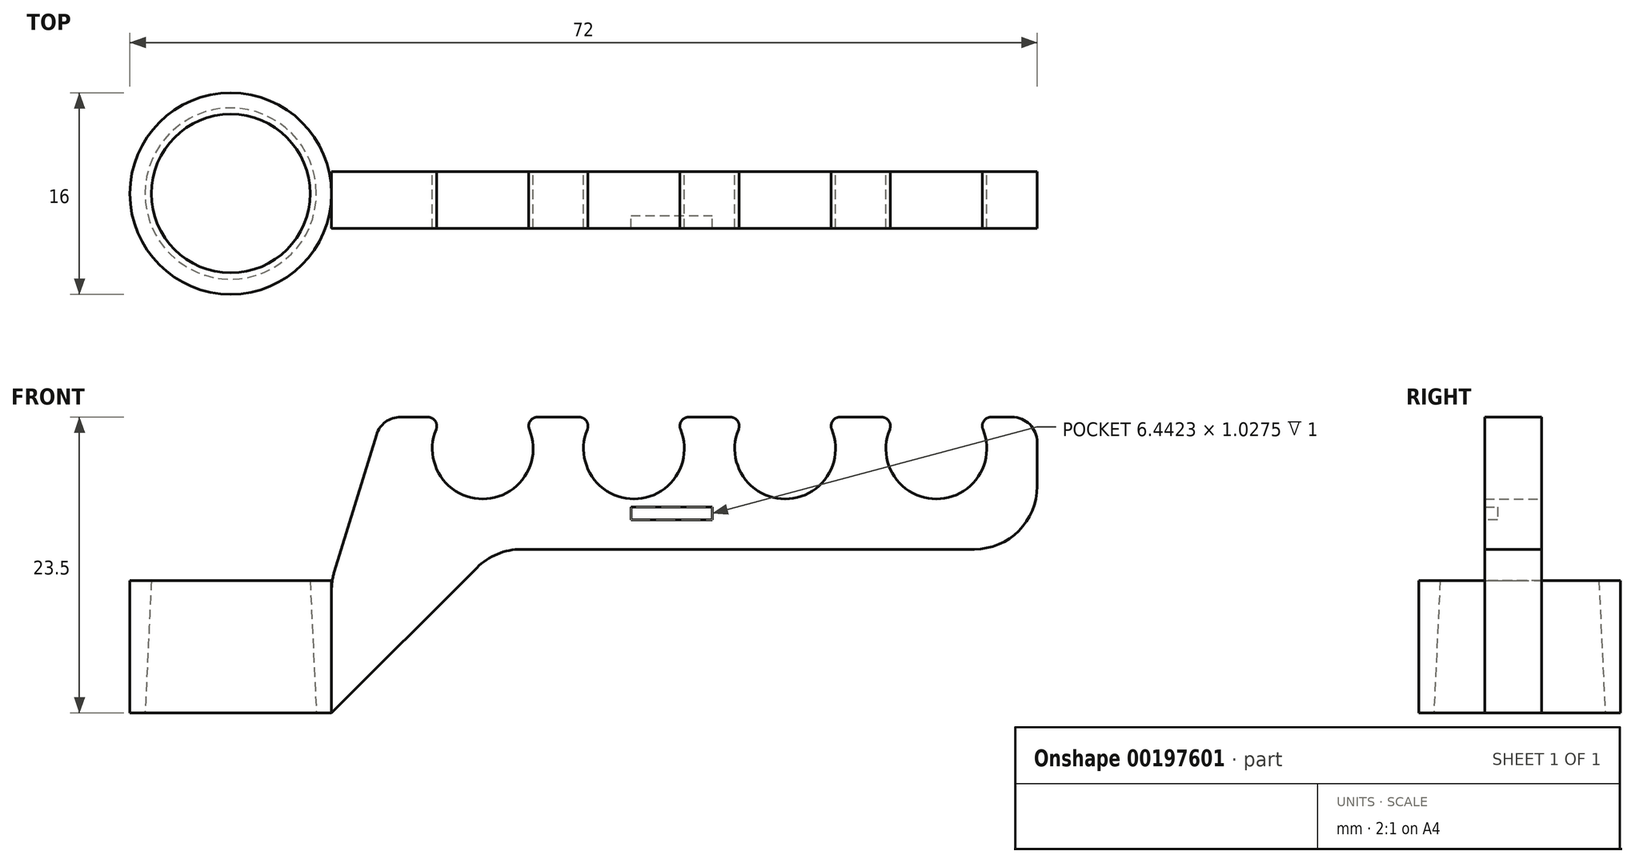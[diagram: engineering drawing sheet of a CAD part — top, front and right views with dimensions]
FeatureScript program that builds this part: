
annotation { "Feature Type Name" : "Feature", "Feature Type Description" : "" }
export const myFeature = defineFeature(function(context is Context, id is Id, definition is map)
    precondition{}
    {
        {
            var Q0;
            Q0=qCreatedBy(makeId("Top.planeOp"),FACE);
            var sketch = newSketch(context, id + "F0", { "sketchPlane" : qUnion([Q0])});
            skCircle(sketch, "E0", {"center": v(0, 0) * mm, "radius": 6.3 * mm});
            skCircle(sketch, "E1", {"center": v(0, 0) * mm, "radius": 8 * mm});
            skCircle(sketch, "E2", {"center": v(0, 0) * mm, "radius": 6.8 * mm});
            skSolve(sketch);
        }
        {
            var Q0;
            Q0=qCreatedBy(makeId("Front.planeOp"),FACE);
            var sketch = newSketch(context, id + "F1", { "sketchPlane" : qUnion([Q0])});
            skLineSegment(sketch, "E3.0", {"start": v(-6.8, 0) * mm, "end": v(6.8, 0) * mm});
            skLineSegment(sketch, "E4.0", {"start": v(-6.3, 0) * mm, "end": v(6.3, 0) * mm});
            skLineSegment(sketch, "E5.0", {"start": v(-8, 0) * mm, "end": v(-5.58, 0) * mm});
            skLineSegment(sketch, "E6", {"start": v(0, 0) * mm, "end": v(0, 10.5) * mm});
            skLineSegment(sketch, "E7.top", {"start": v(-8, 10.5) * mm, "end": v(-6.3, 10.5) * mm});
            skLineSegment(sketch, "E7.left", {"start": v(-8, 0) * mm, "end": v(-8, 10.5) * mm});
            skLineSegment(sketch, "E8", {"start": v(-6.3, 10.5) * mm, "end": v(-6.8, 0) * mm});
            skLineSegment(sketch, "E9.trimOffspring", {"start": v(0, 0) * mm, "end": v(8, 0) * mm});
            skSolve(sketch);
        }
        {
            var Q0;
            Q0=makeQuery(id+"F1.imprint","IMPRINT",FACE,{"disambiguationData":[TD([[makeQuery(id+"F1.imprint","IMPRINT",EDGE,{"derivedFrom":sQuery(id+"F1.wireOp",EDGE,"E7.top")}),-1.0]])]});
            var Q1;
            Q1=sQuery(id+"F1.wireOp",EDGE,"E6");
            revolve(context, id + "F2", {"entities" : qUnion([Q0]), "axis" : qUnion([Q1]), "revolveType" : RevolveType.FULL});
        }
        {
            var Q0;
            Q0=qCreatedBy(makeId("Front.planeOp"),FACE);
            var sketch = newSketch(context, id + "F3", { "sketchPlane" : qUnion([Q0])});
            skLineSegment(sketch, "E10", {"start": v(8, 10.5) * mm, "end": v(8, 0) * mm});
            skLineSegment(sketch, "E11.0", {"start": v(8, 10.5) * mm, "end": v(-8, 10.5) * mm});
            skLineSegment(sketch, "E12.0", {"start": v(-8, 0) * mm, "end": v(8, 0) * mm});
            skLineSegment(sketch, "E13", {"start": v(0, 13) * mm, "end": v(41.13, 13) * mm, "construction": true});
            skLineSegment(sketch, "E14", {"start": v(0, 21) * mm, "end": v(40.48, 21) * mm, "construction": true});
            skLineSegment(sketch, "E15", {"start": v(20, 25.73) * mm, "end": v(20, 4.34) * mm, "construction": true});
            skCircle(sketch, "E16", {"center": v(20, 21) * mm, "radius": 4 * mm});
            skCircle(sketch, "E17.1.0.0", {"center": v(32, 21) * mm, "radius": 4 * mm});
            skCircle(sketch, "E17.2.0.0", {"center": v(44, 21) * mm, "radius": 4 * mm});
            skCircle(sketch, "E17.3.0.0", {"center": v(56, 21) * mm, "radius": 4 * mm});
            skLineSegment(sketch, "E17.direction1", {"start": v(20, 21) * mm, "end": v(32, 21) * mm, "construction": true});
            skLineSegment(sketch, "E18", {"start": v(12, 25.64) * mm, "end": v(12, 16.43) * mm, "construction": true});
            skLineSegment(sketch, "E19", {"start": v(12, 23.5) * mm, "end": v(68.02, 23.5) * mm});
            skLineSegment(sketch, "E20", {"start": v(64, 26.61) * mm, "end": v(64, 15.45) * mm, "construction": true});
            skLineSegment(sketch, "E21", {"start": v(12, 23.5) * mm, "end": v(8, 10.5) * mm});
            skLineSegment(sketch, "E22", {"start": v(22.25, 13) * mm, "end": v(41.13, 13) * mm});
            skLineSegment(sketch, "E23", {"start": v(64, 13) * mm, "end": v(64, 23.5) * mm});
            skLineSegment(sketch, "E24", {"start": v(8, 0) * mm, "end": v(21, 13) * mm});
            skPoint(sketch, "E25.orphan", {"position": v(22.25, 14.25) * mm});
            skLineSegment(sketch, "E26", {"start": v(21, 13) * mm, "end": v(22.25, 13) * mm});
            skLineSegment(sketch, "E27", {"start": v(41.13, 13) * mm, "end": v(64, 13) * mm});
            skLineSegment(sketch, "E28.bottom", {"start": v(8, 10.5) * mm, "end": v(7.8, 10.5) * mm});
            skLineSegment(sketch, "E28.top", {"start": v(8, 0) * mm, "end": v(7.8, 0) * mm});
            skLineSegment(sketch, "E28.right", {"start": v(7.8, 10.5) * mm, "end": v(7.8, 0) * mm});
            skSolve(sketch);
        }
        {
            var Q0;
            {var subQ0=sQuery(id+"F3.wireOp",EDGE,"E21");Q0=makeQuery(id+"F3.imprint","IMPRINT",FACE,{"disambiguationData":[TD([[makeQuery(id+"F3.imprint","IMPRINT",EDGE,{"derivedFrom":subQ0}),1.0]])]});}
            var Q1;
            Q1=makeQuery(id+"F3.imprint","IMPRINT",FACE,{"disambiguationData":[TD([[makeQuery(id+"F3.imprint","IMPRINT",EDGE,{"derivedFrom":sQuery(id+"F3.wireOp",EDGE,"E28.bottom")}),1.0]])]});
            extrude(context, id + "F4", {"entities" : qUnion([Q0, Q1]), "operationType" : NewBodyOperationType.ADD, "endBound" : BoundingType.SYMMETRIC, "depth" : 3.5 * mm});
        }
        {
            var Q0;
            Q0=makeQuery(id+"F4.boolean.opBoolean","INTERSECT",EDGE,{"derivedFrom":[makeQuery(id+"F2.opRevolve","SWEPT_FACE",FACE,{"disambiguationData":[OSD([sQuery(id+"F1.wireOp",EDGE,"E7.left")])]}),makeQuery(id+"F4.opExtrude","CAP_FACE",FACE,{"disambiguationData":[OSD([sQuery(id+"F3.wireOp",EDGE,"E16"),sQuery(id+"F3.wireOp",EDGE,"E17.1.0.0"),sQuery(id+"F3.wireOp",EDGE,"E17.2.0.0"),sQuery(id+"F3.wireOp",EDGE,"E17.3.0.0"),sQuery(id+"F3.wireOp",EDGE,"E19"),sQuery(id+"F3.wireOp",EDGE,"E21"),sQuery(id+"F3.wireOp",EDGE,"E22"),sQuery(id+"F3.wireOp",EDGE,"E23"),sQuery(id+"F3.wireOp",EDGE,"E24"),sQuery(id+"F3.wireOp",EDGE,"E26"),sQuery(id+"F3.wireOp",EDGE,"E27"),sQuery(id+"F3.wireOp",EDGE,"E28.bottom"),sQuery(id+"F3.wireOp",EDGE,"E28.top"),sQuery(id+"F3.wireOp",EDGE,"E28.right")])],"isStart":true})]});
            var Q1;
            Q1=makeQuery(id+"F4.boolean.opBoolean","INTERSECT",EDGE,{"derivedFrom":[makeQuery(id+"F2.opRevolve","SWEPT_FACE",FACE,{"disambiguationData":[OSD([sQuery(id+"F1.wireOp",EDGE,"E7.left")])]}),makeQuery(id+"F4.opExtrude","CAP_FACE",FACE,{"disambiguationData":[OSD([sQuery(id+"F3.wireOp",EDGE,"E16"),sQuery(id+"F3.wireOp",EDGE,"E17.1.0.0"),sQuery(id+"F3.wireOp",EDGE,"E17.2.0.0"),sQuery(id+"F3.wireOp",EDGE,"E17.3.0.0"),sQuery(id+"F3.wireOp",EDGE,"E19"),sQuery(id+"F3.wireOp",EDGE,"E21"),sQuery(id+"F3.wireOp",EDGE,"E22"),sQuery(id+"F3.wireOp",EDGE,"E23"),sQuery(id+"F3.wireOp",EDGE,"E24"),sQuery(id+"F3.wireOp",EDGE,"E26"),sQuery(id+"F3.wireOp",EDGE,"E27"),sQuery(id+"F3.wireOp",EDGE,"E28.bottom"),sQuery(id+"F3.wireOp",EDGE,"E28.top"),sQuery(id+"F3.wireOp",EDGE,"E28.right")])],"isStart":false})]});
            var Q2;
            Q2=makeQuery(id+"F4.opExtrude","SWEPT_EDGE",EDGE,{"disambiguationData":[OSD([sQuery(id+"F3.wireOp",EDGE,"E24"),sQuery(id+"F3.wireOp",EDGE,"E26")])]});
            var Q3;
            Q3=makeQuery(id+"F4.opExtrude","SWEPT_EDGE",EDGE,{"disambiguationData":[OSD([sQuery(id+"F3.wireOp",EDGE,"E23"),sQuery(id+"F3.wireOp",EDGE,"E27")])]});
            fillet(context, id + "F5", {"entities" : qUnion([Q0, Q1, Q2, Q3]), "radius" : 5 * mm, "tangentPropagation" : true, "allowEdgeOverflow" : false});
        }
        {
            var Q0;
            Q0=makeQuery(id+"F4.opExtrude","SWEPT_EDGE",EDGE,{"disambiguationData":[OSD([sQuery(id+"F3.wireOp",EDGE,"E19"),sQuery(id+"F3.wireOp",EDGE,"E21")])]});
            var Q1;
            Q1=makeQuery(id+"F4.opExtrude","SWEPT_EDGE",EDGE,{"disambiguationData":[OSD([sQuery(id+"F3.wireOp",EDGE,"E19"),sQuery(id+"F3.wireOp",EDGE,"E23")])]});
            fillet(context, id + "F6", {"entities" : qUnion([Q0, Q1]), "radius" : 2 * mm, "tangentPropagation" : true, "allowEdgeOverflow" : false});
        }
        {
            var Q0;
            {var subQ0=sQuery(id+"F3.wireOp",EDGE,"E19");var subQ1=sQuery(id+"F3.wireOp",EDGE,"E16");Q0=makeQuery(id+"F4.opExtrude","SWEPT_EDGE",EDGE,{"disambiguationData":[OSD([subQ1,subQ0]),TDD([makeQuery(id+"F3.imprint","INTERSECT",VERTEX,{"disambiguationData":[OD(1.0)],"derivedFrom":[subQ1,subQ0]})])]});}
            var Q1;
            {var subQ0=sQuery(id+"F3.wireOp",EDGE,"E19");var subQ1=sQuery(id+"F3.wireOp",EDGE,"E16");Q1=makeQuery(id+"F4.opExtrude","SWEPT_EDGE",EDGE,{"disambiguationData":[OSD([subQ1,subQ0]),TDD([makeQuery(id+"F3.imprint","INTERSECT",VERTEX,{"disambiguationData":[OD(0.0)],"derivedFrom":[subQ1,subQ0]})])]});}
            var Q2;
            {var subQ0=sQuery(id+"F3.wireOp",EDGE,"E19");var subQ1=sQuery(id+"F3.wireOp",EDGE,"E17.1.0.0");Q2=makeQuery(id+"F4.opExtrude","SWEPT_EDGE",EDGE,{"disambiguationData":[OSD([subQ1,subQ0]),TDD([makeQuery(id+"F3.imprint","INTERSECT",VERTEX,{"disambiguationData":[OD(0.0)],"derivedFrom":[subQ1,subQ0]})])]});}
            var Q3;
            {var subQ0=sQuery(id+"F3.wireOp",EDGE,"E19");var subQ1=sQuery(id+"F3.wireOp",EDGE,"E17.2.0.0");Q3=makeQuery(id+"F4.opExtrude","SWEPT_EDGE",EDGE,{"disambiguationData":[OSD([subQ1,subQ0]),TDD([makeQuery(id+"F3.imprint","INTERSECT",VERTEX,{"disambiguationData":[OD(0.0)],"derivedFrom":[subQ1,subQ0]})])]});}
            var Q4;
            {var subQ0=sQuery(id+"F3.wireOp",EDGE,"E19");var subQ1=sQuery(id+"F3.wireOp",EDGE,"E17.3.0.0");Q4=makeQuery(id+"F4.opExtrude","SWEPT_EDGE",EDGE,{"disambiguationData":[OSD([subQ1,subQ0]),TDD([makeQuery(id+"F3.imprint","INTERSECT",VERTEX,{"disambiguationData":[OD(0.0)],"derivedFrom":[subQ1,subQ0]})])]});}
            var Q5;
            {var subQ0=sQuery(id+"F3.wireOp",EDGE,"E19");var subQ1=sQuery(id+"F3.wireOp",EDGE,"E17.1.0.0");Q5=makeQuery(id+"F4.opExtrude","SWEPT_EDGE",EDGE,{"disambiguationData":[OSD([subQ1,subQ0]),TDD([makeQuery(id+"F3.imprint","INTERSECT",VERTEX,{"disambiguationData":[OD(1.0)],"derivedFrom":[subQ1,subQ0]})])]});}
            var Q6;
            {var subQ0=sQuery(id+"F3.wireOp",EDGE,"E19");var subQ1=sQuery(id+"F3.wireOp",EDGE,"E17.2.0.0");Q6=makeQuery(id+"F4.opExtrude","SWEPT_EDGE",EDGE,{"disambiguationData":[OSD([subQ1,subQ0]),TDD([makeQuery(id+"F3.imprint","INTERSECT",VERTEX,{"disambiguationData":[OD(1.0)],"derivedFrom":[subQ1,subQ0]})])]});}
            var Q7;
            {var subQ0=sQuery(id+"F3.wireOp",EDGE,"E19");var subQ1=sQuery(id+"F3.wireOp",EDGE,"E17.3.0.0");Q7=makeQuery(id+"F4.opExtrude","SWEPT_EDGE",EDGE,{"disambiguationData":[OSD([subQ1,subQ0]),TDD([makeQuery(id+"F3.imprint","INTERSECT",VERTEX,{"disambiguationData":[OD(1.0)],"derivedFrom":[subQ1,subQ0]})])]});}
            fillet(context, id + "F7", {"entities" : qUnion([Q0, Q1, Q2, Q3, Q4, Q5, Q6, Q7]), "radius" : .71 * mm, "tangentPropagation" : true, "allowEdgeOverflow" : false});
        }
        {
            var Q0;
            Q0=makeQuery(id+"F4.opExtrude","CAP_FACE",FACE,{"disambiguationData":[OSD([sQuery(id+"F3.wireOp",EDGE,"E16"),sQuery(id+"F3.wireOp",EDGE,"E17.1.0.0"),sQuery(id+"F3.wireOp",EDGE,"E17.2.0.0"),sQuery(id+"F3.wireOp",EDGE,"E17.3.0.0"),sQuery(id+"F3.wireOp",EDGE,"E19"),sQuery(id+"F3.wireOp",EDGE,"E21"),sQuery(id+"F3.wireOp",EDGE,"E22"),sQuery(id+"F3.wireOp",EDGE,"E23"),sQuery(id+"F3.wireOp",EDGE,"E24"),sQuery(id+"F3.wireOp",EDGE,"E26"),sQuery(id+"F3.wireOp",EDGE,"E27"),sQuery(id+"F3.wireOp",EDGE,"E28.bottom"),sQuery(id+"F3.wireOp",EDGE,"E28.top"),sQuery(id+"F3.wireOp",EDGE,"E28.right")])],"isStart":false});
            var sketch = newSketch(context, id + "F8", { "sketchPlane" : qUnion([Q0])});
            skFitSpline(sketch, "E29", {"points": [v(35.71, 16.35) * mm, v(35.78, 16.55) * mm, v(35.85, 16.65) * mm, v(35.98, 16.75) * mm, v(36.12, 16.8) * mm, v(36.24, 16.8) * mm, v(42.55, 16.82) * mm, v(42.65, 16.78) * mm, v(42.7, 16.65) * mm, v(42.65, 16.52) * mm, v(42.55, 16.36) * mm, v(42.42, 16.32) * mm, v(42.3, 16.26) * mm, v(42.08, 15.9) * mm, v(41.89, 15.83) * mm, v(41.78, 15.76) * mm, v(41.62, 15.48) * mm, v(41.45, 15.38) * mm, v(38.77, 14.57) * mm, v(38.7, 14.56) * mm, v(38.62, 14.38) * mm, v(38.56, 14.27) * mm, v(38.18, 14.06) * mm, v(38.06, 14.02) * mm, v(35.9, 13.44) * mm, v(35.75, 13.44) * mm, v(35.65, 13.48) * mm, v(35.59, 13.53) * mm, v(35, 14.06) * mm, v(34.97, 14.05) * mm, v(34.9, 14.03) * mm, v(34.85, 14) * mm, v(34.31, 13.47) * mm, v(34.24, 13.44) * mm, v(34.16, 13.44) * mm, v(31.77, 14.07) * mm, v(31.41, 14.28) * mm, v(31.3, 14.48) * mm, v(31.22, 14.57) * mm, v(31.12, 14.6) * mm, v(28.44, 15.4) * mm, v(28.33, 15.52) * mm, v(28.2, 15.88) * mm, v(28.14, 15.83) * mm, v(28.02, 15.85) * mm, v(27.94, 15.87) * mm, v(27.88, 15.92) * mm, v(27.69, 16.27) * mm, v(27.65, 16.3) * mm, v(27.51, 16.3) * mm, v(27.46, 16.32) * mm, v(27.28, 16.62) * mm, v(27.28, 16.7) * mm, v(27.33, 16.77) * mm, v(27.4, 16.8) * mm, v(27.46, 16.8) * mm, v(33.8, 16.81) * mm, v(33.85, 16.81) * mm, v(33.97, 16.77) * mm, v(34.17, 16.6) * mm, v(34.2, 16.5) * mm, v(34.25, 16.4) * mm, v(34.26, 16.34) * mm, v(34.33, 16.34) * mm, v(35.58, 16.34) * mm, v(35.71, 16.35) * mm]});
            skFitSpline(sketch, "E30", {"points": [v(30.68, 16.8) * mm, v(30.83, 16.69) * mm, v(30.9, 16.62) * mm, v(30.99, 16.5) * mm, v(31.06, 16.33) * mm, v(31.28, 16.02) * mm, v(31.53, 15.67) * mm, v(31.6, 15.6) * mm, v(32.13, 15.09) * mm, v(32.73, 14.67) * mm, v(33.36, 14.37) * mm, v(33.87, 14.2) * mm, v(34.55, 14.1) * mm, v(35, 14.06) * mm, v(35.61, 14.1) * mm, v(36.24, 14.24) * mm, v(36.81, 14.44) * mm, v(37.3, 14.7) * mm, v(37.8, 15.05) * mm, v(38.1, 15.33) * mm, v(38.48, 15.75) * mm, v(38.72, 16.05) * mm, v(38.93, 16.39) * mm, v(39.08, 16.63) * mm, v(39.22, 16.76) * mm, v(39.4, 16.82) * mm, v(39.46, 16.82) * mm], "startDerivative": vector(6.61, -4.14) * mm, "endDerivative": vector(2.94, -0.27) * mm});
            skLineSegment(sketch, "E31.bottom", {"start": v(31.76, 16.35) * mm, "end": v(38.2, 16.35) * mm});
            skLineSegment(sketch, "E31.top", {"start": v(31.76, 15.33) * mm, "end": v(38.2, 15.33) * mm});
            skLineSegment(sketch, "E31.left", {"start": v(31.76, 16.35) * mm, "end": v(31.76, 15.33) * mm});
            skLineSegment(sketch, "E31.right", {"start": v(38.2, 16.35) * mm, "end": v(38.2, 15.33) * mm});
            skLineSegment(sketch, "E32", {"start": v(27.69, 16.27) * mm, "end": v(31.76, 16.35) * mm});
            skLineSegment(sketch, "E33", {"start": v(31.76, 16.1) * mm, "end": v(28.2, 15.88) * mm});
            skLineSegment(sketch, "E34", {"start": v(31.76, 15.88) * mm, "end": v(28.44, 15.4) * mm});
            skLineSegment(sketch, "E35", {"start": v(31.76, 15.67) * mm, "end": v(29.25, 15.15) * mm});
            skLineSegment(sketch, "E36", {"start": v(31.76, 15.33) * mm, "end": v(30.28, 14.84) * mm});
            skLineSegment(sketch, "E37", {"start": v(32.82, 15.33) * mm, "end": v(31.22, 14.57) * mm});
            skLineSegment(sketch, "E38", {"start": v(33.59, 15.33) * mm, "end": v(31.77, 14.07) * mm});
            skLineSegment(sketch, "E39", {"start": v(34.05, 15.33) * mm, "end": v(32.59, 13.83) * mm});
            skLineSegment(sketch, "E40", {"start": v(34.4, 15.33) * mm, "end": v(33.39, 13.61) * mm});
            skLineSegment(sketch, "E41", {"start": v(34.73, 15.33) * mm, "end": v(34.16, 13.44) * mm});
            skLineSegment(sketch, "E42", {"start": v(34.98, 15.33) * mm, "end": v(34.97, 14.05) * mm});
            skLineSegment(sketch, "E43", {"start": v(35.26, 15.33) * mm, "end": v(35.81, 13.43) * mm});
            skLineSegment(sketch, "E44", {"start": v(35.61, 15.33) * mm, "end": v(36.58, 13.6) * mm});
            skLineSegment(sketch, "E45", {"start": v(35.96, 15.33) * mm, "end": v(37.37, 13.83) * mm});
            skLineSegment(sketch, "E46", {"start": v(36.38, 15.33) * mm, "end": v(38.18, 14.06) * mm});
            skLineSegment(sketch, "E47", {"start": v(37.14, 15.33) * mm, "end": v(38.77, 14.57) * mm});
            skLineSegment(sketch, "E48", {"start": v(38.2, 15.33) * mm, "end": v(39.77, 14.85) * mm});
            skLineSegment(sketch, "E49", {"start": v(38.2, 15.65) * mm, "end": v(40.68, 15.13) * mm});
            skLineSegment(sketch, "E50", {"start": v(38.2, 15.87) * mm, "end": v(41.57, 15.43) * mm});
            skLineSegment(sketch, "E51", {"start": v(38.2, 16.1) * mm, "end": v(42.02, 15.86) * mm});
            skLineSegment(sketch, "E52", {"start": v(38.2, 16.3) * mm, "end": v(42.35, 16.3) * mm});
            skSolve(sketch);
        }
        {
            var Q0;
            {var subQ0=sQuery(id+"F8.wireOp",EDGE,"E36");Q0=makeQuery(id+"F8.imprint","IMPRINT",FACE,{"disambiguationData":[TD([[makeQuery(id+"F8.imprint","IMPRINT",EDGE,{"derivedFrom":subQ0}),-1.0]])]});}
            var Q1;
            {var subQ0=sQuery(id+"F8.wireOp",EDGE,"E46");var subQ1=sQuery(id+"F8.wireOp",EDGE,"E29");var subQ2=makeQuery(id+"F8.imprint","INTERSECT",VERTEX,{"derivedFrom":[subQ1,subQ0]});Q1=makeQuery(id+"F8.imprint","IMPRINT",FACE,{"disambiguationData":[TD([[makeQuery(id+"F8.imprint","IMPRINT",EDGE,{"disambiguationData":[TD([[subQ2,1.0]])],"derivedFrom":subQ1}),-1.0]])]});}
            var Q2;
            {var subQ0=sQuery(id+"F8.wireOp",EDGE,"E38");var subQ1=sQuery(id+"F8.wireOp",EDGE,"E29");var subQ2=makeQuery(id+"F8.imprint","INTERSECT",VERTEX,{"derivedFrom":[subQ1,subQ0]});Q2=makeQuery(id+"F8.imprint","IMPRINT",FACE,{"disambiguationData":[TD([[makeQuery(id+"F8.imprint","IMPRINT",EDGE,{"disambiguationData":[TD([[subQ2,1.0]])],"derivedFrom":subQ1}),-1.0]])]});}
            var Q3;
            {var subQ0=sQuery(id+"F8.wireOp",EDGE,"E44");var subQ1=sQuery(id+"F8.wireOp",EDGE,"E30");var subQ2=makeQuery(id+"F8.imprint","INTERSECT",VERTEX,{"derivedFrom":[subQ1,subQ0]});Q3=makeQuery(id+"F8.imprint","IMPRINT",FACE,{"disambiguationData":[TD([[makeQuery(id+"F8.imprint","IMPRINT",EDGE,{"disambiguationData":[TD([[subQ2,-1.0]])],"derivedFrom":subQ1}),1.0]])]});}
            var Q4;
            {var subQ0=sQuery(id+"F8.wireOp",EDGE,"E39");var subQ1=sQuery(id+"F8.wireOp",EDGE,"E29");var subQ2=makeQuery(id+"F8.imprint","INTERSECT",VERTEX,{"derivedFrom":[subQ1,subQ0]});Q4=makeQuery(id+"F8.imprint","IMPRINT",FACE,{"disambiguationData":[TD([[makeQuery(id+"F8.imprint","IMPRINT",EDGE,{"disambiguationData":[TD([[subQ2,1.0]])],"derivedFrom":subQ1}),-1.0]])]});}
            var Q5;
            {var subQ0=sQuery(id+"F8.wireOp",EDGE,"E43");var subQ1=sQuery(id+"F8.wireOp",EDGE,"E30");var subQ2=makeQuery(id+"F8.imprint","INTERSECT",VERTEX,{"derivedFrom":[subQ1,subQ0]});Q5=makeQuery(id+"F8.imprint","IMPRINT",FACE,{"disambiguationData":[TD([[makeQuery(id+"F8.imprint","IMPRINT",EDGE,{"disambiguationData":[TD([[subQ2,-1.0]])],"derivedFrom":subQ1}),1.0]])]});}
            var Q6;
            {var subQ0=sQuery(id+"F8.wireOp",EDGE,"E30");var subQ1=sQuery(id+"F8.wireOp",EDGE,"E29");var subQ2=makeQuery(id+"F8.imprint","INTERSECT",VERTEX,{"disambiguationData":[OD(0.0)],"derivedFrom":[subQ1,subQ0]});Q6=makeQuery(id+"F8.imprint","IMPRINT",FACE,{"disambiguationData":[TD([[makeQuery(id+"F8.imprint","IMPRINT",EDGE,{"disambiguationData":[TD([[subQ2,-1.0]])],"derivedFrom":subQ1}),-1.0]])]});}
            var Q7;
            {var subQ0=sQuery(id+"F8.wireOp",EDGE,"E41");var subQ1=sQuery(id+"F8.wireOp",EDGE,"E30");var subQ2=makeQuery(id+"F8.imprint","INTERSECT",VERTEX,{"derivedFrom":[subQ1,subQ0]});Q7=makeQuery(id+"F8.imprint","IMPRINT",FACE,{"disambiguationData":[TD([[makeQuery(id+"F8.imprint","IMPRINT",EDGE,{"disambiguationData":[TD([[subQ2,-1.0]])],"derivedFrom":subQ1}),1.0]])]});}
            var Q8;
            {var subQ0=sQuery(id+"F8.wireOp",EDGE,"E32");var subQ1=sQuery(id+"F8.wireOp",EDGE,"E30");var subQ2=makeQuery(id+"F8.imprint","INTERSECT",VERTEX,{"derivedFrom":[subQ1,subQ0]});Q8=makeQuery(id+"F8.imprint","IMPRINT",FACE,{"disambiguationData":[TD([[makeQuery(id+"F8.imprint","IMPRINT",EDGE,{"disambiguationData":[TD([[subQ2,-1.0]])],"derivedFrom":subQ1}),1.0]])]});}
            var Q9;
            {var subQ0=sQuery(id+"F8.wireOp",EDGE,"E48");Q9=makeQuery(id+"F8.imprint","IMPRINT",FACE,{"disambiguationData":[TD([[makeQuery(id+"F8.imprint","IMPRINT",EDGE,{"derivedFrom":subQ0}),-1.0]])]});}
            var Q10;
            {var subQ0=sQuery(id+"F8.wireOp",EDGE,"E32");var subQ1=sQuery(id+"F8.wireOp",EDGE,"E29");var subQ2=makeQuery(id+"F8.imprint","INTERSECT",VERTEX,{"derivedFrom":[subQ1,subQ0]});Q10=makeQuery(id+"F8.imprint","IMPRINT",FACE,{"disambiguationData":[TD([[makeQuery(id+"F8.imprint","IMPRINT",EDGE,{"disambiguationData":[TD([[subQ2,1.0]])],"derivedFrom":subQ1}),-1.0]])]});}
            var Q11;
            {var subQ0=sQuery(id+"F8.wireOp",EDGE,"E40");var subQ1=sQuery(id+"F8.wireOp",EDGE,"E30");var subQ2=makeQuery(id+"F8.imprint","INTERSECT",VERTEX,{"derivedFrom":[subQ1,subQ0]});Q11=makeQuery(id+"F8.imprint","IMPRINT",FACE,{"disambiguationData":[TD([[makeQuery(id+"F8.imprint","IMPRINT",EDGE,{"disambiguationData":[TD([[subQ2,-1.0]])],"derivedFrom":subQ1}),1.0]])]});}
            var Q12;
            {var subQ3=sQuery(id+"F8.wireOp",EDGE,"E29");var subQ7=sQuery(id+"F8.wireOp",EDGE,"E30");var subQ8=makeQuery(id+"F8.imprint","INTERSECT",VERTEX,{"disambiguationData":[OD(2.0)],"derivedFrom":[subQ3,subQ7]});Q12=makeQuery(id+"F8.imprint","IMPRINT",FACE,{"disambiguationData":[TD([[makeQuery(id+"F8.imprint","IMPRINT",EDGE,{"disambiguationData":[TD([[subQ8,1.0]])],"derivedFrom":subQ3}),-1.0]])]});}
            var Q13;
            {var subQ0=sQuery(id+"F8.wireOp",EDGE,"E48");Q13=makeQuery(id+"F8.imprint","IMPRINT",FACE,{"disambiguationData":[TD([[makeQuery(id+"F8.imprint","IMPRINT",EDGE,{"derivedFrom":subQ0}),1.0]])]});}
            var Q14;
            {var subQ0=sQuery(id+"F8.wireOp",EDGE,"E33");var subQ1=sQuery(id+"F8.wireOp",EDGE,"E29");var subQ2=makeQuery(id+"F8.imprint","INTERSECT",VERTEX,{"derivedFrom":[subQ1,subQ0]});Q14=makeQuery(id+"F8.imprint","IMPRINT",FACE,{"disambiguationData":[TD([[makeQuery(id+"F8.imprint","IMPRINT",EDGE,{"disambiguationData":[TD([[subQ2,1.0]])],"derivedFrom":subQ1}),-1.0]])]});}
            var Q15;
            {var subQ0=sQuery(id+"F8.wireOp",EDGE,"E39");var subQ1=sQuery(id+"F8.wireOp",EDGE,"E30");var subQ2=makeQuery(id+"F8.imprint","INTERSECT",VERTEX,{"derivedFrom":[subQ1,subQ0]});Q15=makeQuery(id+"F8.imprint","IMPRINT",FACE,{"disambiguationData":[TD([[makeQuery(id+"F8.imprint","IMPRINT",EDGE,{"disambiguationData":[TD([[subQ2,-1.0]])],"derivedFrom":subQ1}),1.0]])]});}
            var Q16;
            {var subQ0=sQuery(id+"F8.wireOp",EDGE,"E34");var subQ1=sQuery(id+"F8.wireOp",EDGE,"E29");var subQ2=makeQuery(id+"F8.imprint","INTERSECT",VERTEX,{"derivedFrom":[subQ1,subQ0]});Q16=makeQuery(id+"F8.imprint","IMPRINT",FACE,{"disambiguationData":[TD([[makeQuery(id+"F8.imprint","IMPRINT",EDGE,{"disambiguationData":[TD([[subQ2,1.0]])],"derivedFrom":subQ1}),-1.0]])]});}
            var Q17;
            {var subQ0=sQuery(id+"F8.wireOp",EDGE,"E46");var subQ1=sQuery(id+"F8.wireOp",EDGE,"E30");var subQ2=makeQuery(id+"F8.imprint","INTERSECT",VERTEX,{"derivedFrom":[subQ1,subQ0]});Q17=makeQuery(id+"F8.imprint","IMPRINT",FACE,{"disambiguationData":[TD([[makeQuery(id+"F8.imprint","IMPRINT",EDGE,{"disambiguationData":[TD([[subQ2,-1.0]])],"derivedFrom":subQ1}),1.0]])]});}
            var Q18;
            {var subQ0=sQuery(id+"F8.wireOp",EDGE,"E38");var subQ1=sQuery(id+"F8.wireOp",EDGE,"E30");var subQ2=makeQuery(id+"F8.imprint","INTERSECT",VERTEX,{"derivedFrom":[subQ1,subQ0]});Q18=makeQuery(id+"F8.imprint","IMPRINT",FACE,{"disambiguationData":[TD([[makeQuery(id+"F8.imprint","IMPRINT",EDGE,{"disambiguationData":[TD([[subQ2,-1.0]])],"derivedFrom":subQ1}),1.0]])]});}
            var Q19;
            {var subQ0=sQuery(id+"F8.wireOp",EDGE,"E36");Q19=makeQuery(id+"F8.imprint","IMPRINT",FACE,{"disambiguationData":[TD([[makeQuery(id+"F8.imprint","IMPRINT",EDGE,{"derivedFrom":subQ0}),1.0]])]});}
            var Q20;
            {var subQ0=sQuery(id+"F8.wireOp",EDGE,"E44");var subQ1=sQuery(id+"F8.wireOp",EDGE,"E29");var subQ2=makeQuery(id+"F8.imprint","INTERSECT",VERTEX,{"derivedFrom":[subQ1,subQ0]});Q20=makeQuery(id+"F8.imprint","IMPRINT",FACE,{"disambiguationData":[TD([[makeQuery(id+"F8.imprint","IMPRINT",EDGE,{"disambiguationData":[TD([[subQ2,1.0]])],"derivedFrom":subQ1}),-1.0]])]});}
            var Q21;
            {var subQ0=sQuery(id+"F8.wireOp",EDGE,"E37");var subQ1=sQuery(id+"F8.wireOp",EDGE,"E30");var subQ2=makeQuery(id+"F8.imprint","INTERSECT",VERTEX,{"derivedFrom":[subQ1,subQ0]});Q21=makeQuery(id+"F8.imprint","IMPRINT",FACE,{"disambiguationData":[TD([[makeQuery(id+"F8.imprint","IMPRINT",EDGE,{"disambiguationData":[TD([[subQ2,-1.0]])],"derivedFrom":subQ1}),1.0]])]});}
            var Q22;
            {var subQ5=sQuery(id+"F8.wireOp",EDGE,"E30");var subQ6=sQuery(id+"F8.wireOp",EDGE,"E29");var subQ9=makeQuery(id+"F8.imprint","INTERSECT",VERTEX,{"disambiguationData":[OD(3.0)],"derivedFrom":[subQ6,subQ5]});Q22=makeQuery(id+"F8.imprint","IMPRINT",FACE,{"disambiguationData":[TD([[makeQuery(id+"F8.imprint","IMPRINT",EDGE,{"disambiguationData":[TD([[subQ9,-1.0]])],"derivedFrom":subQ6}),-1.0]])]});}
            var Q23;
            {var subQ0=sQuery(id+"F8.wireOp",EDGE,"E45");var subQ1=sQuery(id+"F8.wireOp",EDGE,"E29");var subQ2=makeQuery(id+"F8.imprint","INTERSECT",VERTEX,{"derivedFrom":[subQ1,subQ0]});Q23=makeQuery(id+"F8.imprint","IMPRINT",FACE,{"disambiguationData":[TD([[makeQuery(id+"F8.imprint","IMPRINT",EDGE,{"disambiguationData":[TD([[subQ2,1.0]])],"derivedFrom":subQ1}),-1.0]])]});}
            var Q24;
            {var subQ0=sQuery(id+"F8.wireOp",EDGE,"E30");var subQ1=sQuery(id+"F8.wireOp",EDGE,"E29");var subQ2=makeQuery(id+"F8.imprint","INTERSECT",VERTEX,{"disambiguationData":[OD(1.0)],"derivedFrom":[subQ1,subQ0]});Q24=makeQuery(id+"F8.imprint","IMPRINT",FACE,{"disambiguationData":[TD([[makeQuery(id+"F8.imprint","IMPRINT",EDGE,{"disambiguationData":[TD([[subQ2,1.0]])],"derivedFrom":subQ1}),-1.0]])]});}
            var Q25;
            {var subQ0=sQuery(id+"F8.wireOp",EDGE,"E47");var subQ1=sQuery(id+"F8.wireOp",EDGE,"E30");var subQ2=makeQuery(id+"F8.imprint","INTERSECT",VERTEX,{"derivedFrom":[subQ1,subQ0]});Q25=makeQuery(id+"F8.imprint","IMPRINT",FACE,{"disambiguationData":[TD([[makeQuery(id+"F8.imprint","IMPRINT",EDGE,{"disambiguationData":[TD([[subQ2,-1.0]])],"derivedFrom":subQ1}),1.0]])]});}
            var Q26;
            {var subQ0=sQuery(id+"F8.wireOp",EDGE,"E37");var subQ1=sQuery(id+"F8.wireOp",EDGE,"E29");var subQ2=makeQuery(id+"F8.imprint","INTERSECT",VERTEX,{"derivedFrom":[subQ1,subQ0]});Q26=makeQuery(id+"F8.imprint","IMPRINT",FACE,{"disambiguationData":[TD([[makeQuery(id+"F8.imprint","IMPRINT",EDGE,{"disambiguationData":[TD([[subQ2,1.0]])],"derivedFrom":subQ1}),-1.0]])]});}
            var Q27;
            {var subQ0=sQuery(id+"F8.wireOp",EDGE,"E45");var subQ1=sQuery(id+"F8.wireOp",EDGE,"E30");var subQ2=makeQuery(id+"F8.imprint","INTERSECT",VERTEX,{"derivedFrom":[subQ1,subQ0]});Q27=makeQuery(id+"F8.imprint","IMPRINT",FACE,{"disambiguationData":[TD([[makeQuery(id+"F8.imprint","IMPRINT",EDGE,{"disambiguationData":[TD([[subQ2,-1.0]])],"derivedFrom":subQ1}),1.0]])]});}
            var Q28;
            {var subQ0=sQuery(id+"F8.wireOp",EDGE,"E30");var subQ1=sQuery(id+"F8.wireOp",EDGE,"E29");var subQ2=makeQuery(id+"F8.imprint","INTERSECT",VERTEX,{"disambiguationData":[OD(0.0)],"derivedFrom":[subQ1,subQ0]});Q28=makeQuery(id+"F8.imprint","IMPRINT",FACE,{"disambiguationData":[TD([[makeQuery(id+"F8.imprint","IMPRINT",EDGE,{"disambiguationData":[TD([[subQ2,1.0]])],"derivedFrom":subQ1}),-1.0]])]});}
            var Q29;
            {var subQ0=sQuery(id+"F8.wireOp",EDGE,"E31.bottom");var subQ1=sQuery(id+"F8.wireOp",EDGE,"E29");var subQ2=makeQuery(id+"F8.imprint","INTERSECT",VERTEX,{"disambiguationData":[OD(0.0)],"derivedFrom":[subQ1,subQ0]});Q29=makeQuery(id+"F8.imprint","IMPRINT",FACE,{"disambiguationData":[TD([[makeQuery(id+"F8.imprint","IMPRINT",EDGE,{"disambiguationData":[TD([[subQ2,-1.0]])],"derivedFrom":subQ1}),1.0]])]});}
            var Q30;
            {var subQ0=sQuery(id+"F8.wireOp",EDGE,"E50");var subQ1=sQuery(id+"F8.wireOp",EDGE,"E29");var subQ2=makeQuery(id+"F8.imprint","INTERSECT",VERTEX,{"derivedFrom":[subQ1,subQ0]});Q30=makeQuery(id+"F8.imprint","IMPRINT",FACE,{"disambiguationData":[TD([[makeQuery(id+"F8.imprint","IMPRINT",EDGE,{"disambiguationData":[TD([[subQ2,1.0]])],"derivedFrom":subQ1}),-1.0]])]});}
            var Q31;
            {var subQ0=sQuery(id+"F8.wireOp",EDGE,"E51");var subQ1=sQuery(id+"F8.wireOp",EDGE,"E29");var subQ2=makeQuery(id+"F8.imprint","INTERSECT",VERTEX,{"derivedFrom":[subQ1,subQ0]});Q31=makeQuery(id+"F8.imprint","IMPRINT",FACE,{"disambiguationData":[TD([[makeQuery(id+"F8.imprint","IMPRINT",EDGE,{"disambiguationData":[TD([[subQ2,1.0]])],"derivedFrom":subQ1}),-1.0]])]});}
            var Q32;
            {var subQ0=sQuery(id+"F8.wireOp",EDGE,"E49");var subQ1=sQuery(id+"F8.wireOp",EDGE,"E29");var subQ2=makeQuery(id+"F8.imprint","INTERSECT",VERTEX,{"derivedFrom":[subQ1,subQ0]});Q32=makeQuery(id+"F8.imprint","IMPRINT",FACE,{"disambiguationData":[TD([[makeQuery(id+"F8.imprint","IMPRINT",EDGE,{"disambiguationData":[TD([[subQ2,1.0]])],"derivedFrom":subQ1}),-1.0]])]});}
            var Q33;
            {var subQ0=sQuery(id+"F8.wireOp",EDGE,"E51");var subQ1=sQuery(id+"F8.wireOp",EDGE,"E30");var subQ2=makeQuery(id+"F8.imprint","INTERSECT",VERTEX,{"derivedFrom":[subQ1,subQ0]});Q33=makeQuery(id+"F8.imprint","IMPRINT",FACE,{"disambiguationData":[TD([[makeQuery(id+"F8.imprint","IMPRINT",EDGE,{"disambiguationData":[TD([[subQ2,-1.0]])],"derivedFrom":subQ1}),1.0]])]});}
            var Q34;
            {var subQ0=sQuery(id+"F8.wireOp",EDGE,"E50");var subQ1=sQuery(id+"F8.wireOp",EDGE,"E30");var subQ2=makeQuery(id+"F8.imprint","INTERSECT",VERTEX,{"derivedFrom":[subQ1,subQ0]});Q34=makeQuery(id+"F8.imprint","IMPRINT",FACE,{"disambiguationData":[TD([[makeQuery(id+"F8.imprint","IMPRINT",EDGE,{"disambiguationData":[TD([[subQ2,-1.0]])],"derivedFrom":subQ1}),1.0]])]});}
            var Q35;
            {var subQ0=sQuery(id+"F8.wireOp",EDGE,"E49");var subQ1=sQuery(id+"F8.wireOp",EDGE,"E30");var subQ2=makeQuery(id+"F8.imprint","INTERSECT",VERTEX,{"derivedFrom":[subQ1,subQ0]});Q35=makeQuery(id+"F8.imprint","IMPRINT",FACE,{"disambiguationData":[TD([[makeQuery(id+"F8.imprint","IMPRINT",EDGE,{"disambiguationData":[TD([[subQ2,-1.0]])],"derivedFrom":subQ1}),1.0]])]});}
            var Q36;
            {var subQ0=sQuery(id+"F8.wireOp",EDGE,"E33");var subQ1=sQuery(id+"F8.wireOp",EDGE,"E30");var subQ2=makeQuery(id+"F8.imprint","INTERSECT",VERTEX,{"derivedFrom":[subQ1,subQ0]});Q36=makeQuery(id+"F8.imprint","IMPRINT",FACE,{"disambiguationData":[TD([[makeQuery(id+"F8.imprint","IMPRINT",EDGE,{"disambiguationData":[TD([[subQ2,-1.0]])],"derivedFrom":subQ1}),1.0]])]});}
            var Q37;
            {var subQ0=sQuery(id+"F8.wireOp",EDGE,"E31.top");var subQ1=sQuery(id+"F8.wireOp",EDGE,"E30");var subQ2=makeQuery(id+"F8.imprint","INTERSECT",VERTEX,{"disambiguationData":[OD(0.0)],"derivedFrom":[subQ1,subQ0]});Q37=makeQuery(id+"F8.imprint","IMPRINT",FACE,{"disambiguationData":[TD([[makeQuery(id+"F8.imprint","IMPRINT",EDGE,{"disambiguationData":[TD([[subQ2,-1.0]])],"derivedFrom":subQ1}),1.0]])]});}
            var Q38;
            {var subQ0=sQuery(id+"F8.wireOp",EDGE,"E34");var subQ1=sQuery(id+"F8.wireOp",EDGE,"E30");var subQ2=makeQuery(id+"F8.imprint","INTERSECT",VERTEX,{"derivedFrom":[subQ1,subQ0]});Q38=makeQuery(id+"F8.imprint","IMPRINT",FACE,{"disambiguationData":[TD([[makeQuery(id+"F8.imprint","IMPRINT",EDGE,{"disambiguationData":[TD([[subQ2,-1.0]])],"derivedFrom":subQ1}),1.0]])]});}
            var Q39;
            {var subQ0=sQuery(id+"F8.wireOp",EDGE,"E31.right");var subQ1=sQuery(id+"F8.wireOp",EDGE,"E30");var subQ2=makeQuery(id+"F8.imprint","INTERSECT",VERTEX,{"derivedFrom":[subQ1,subQ0]});Q39=makeQuery(id+"F8.imprint","IMPRINT",FACE,{"disambiguationData":[TD([[makeQuery(id+"F8.imprint","IMPRINT",EDGE,{"disambiguationData":[TD([[subQ2,-1.0]])],"derivedFrom":subQ1}),1.0]])]});}
            var Q40;
            {var subQ0=sQuery(id+"F8.wireOp",EDGE,"E35");var subQ1=sQuery(id+"F8.wireOp",EDGE,"E30");var subQ2=makeQuery(id+"F8.imprint","INTERSECT",VERTEX,{"derivedFrom":[subQ1,subQ0]});Q40=makeQuery(id+"F8.imprint","IMPRINT",FACE,{"disambiguationData":[TD([[makeQuery(id+"F8.imprint","IMPRINT",EDGE,{"disambiguationData":[TD([[subQ2,-1.0]])],"derivedFrom":subQ1}),1.0]])]});}
            var Q41;
            {var subQ0=sQuery(id+"F8.wireOp",EDGE,"E30");var subQ1=sQuery(id+"F8.wireOp",EDGE,"E29");var subQ2=makeQuery(id+"F8.imprint","INTERSECT",VERTEX,{"disambiguationData":[OD(1.0)],"derivedFrom":[subQ1,subQ0]});Q41=makeQuery(id+"F8.imprint","IMPRINT",FACE,{"disambiguationData":[TD([[makeQuery(id+"F8.imprint","IMPRINT",EDGE,{"disambiguationData":[TD([[subQ2,1.0]])],"derivedFrom":subQ1}),1.0]])]});}
            var Q42;
            {var subQ0=sQuery(id+"F8.wireOp",EDGE,"E31.top");var subQ1=sQuery(id+"F8.wireOp",EDGE,"E30");var subQ2=makeQuery(id+"F8.imprint","INTERSECT",VERTEX,{"disambiguationData":[OD(1.0)],"derivedFrom":[subQ1,subQ0]});Q42=makeQuery(id+"F8.imprint","IMPRINT",FACE,{"disambiguationData":[TD([[makeQuery(id+"F8.imprint","IMPRINT",EDGE,{"disambiguationData":[TD([[subQ2,-1.0]])],"derivedFrom":subQ1}),-1.0]])]});}
            var Q43;
            {var subQ0=sQuery(id+"F8.wireOp",EDGE,"E31.left");var subQ1=sQuery(id+"F8.wireOp",EDGE,"E30");var subQ2=makeQuery(id+"F8.imprint","INTERSECT",VERTEX,{"derivedFrom":[subQ1,subQ0]});Q43=makeQuery(id+"F8.imprint","IMPRINT",FACE,{"disambiguationData":[TD([[makeQuery(id+"F8.imprint","IMPRINT",EDGE,{"disambiguationData":[TD([[subQ2,-1.0]])],"derivedFrom":subQ1}),-1.0]])]});}
            var Q44;
            {var subQ0=sQuery(id+"F8.wireOp",EDGE,"E30");var subQ1=sQuery(id+"F8.wireOp",EDGE,"E29");var subQ2=makeQuery(id+"F8.imprint","INTERSECT",VERTEX,{"disambiguationData":[OD(3.0)],"derivedFrom":[subQ1,subQ0]});Q44=makeQuery(id+"F8.imprint","IMPRINT",FACE,{"disambiguationData":[TD([[makeQuery(id+"F8.imprint","IMPRINT",EDGE,{"disambiguationData":[TD([[subQ2,-1.0]])],"derivedFrom":subQ1}),1.0]])]});}
            var Q45;
            {var subQ0=sQuery(id+"F8.wireOp",EDGE,"E42");var subQ1=sQuery(id+"F8.wireOp",EDGE,"E29");var subQ2=makeQuery(id+"F8.imprint","INTERSECT",VERTEX,{"derivedFrom":[subQ1,subQ0]});Q45=makeQuery(id+"F8.imprint","IMPRINT",FACE,{"disambiguationData":[TD([[makeQuery(id+"F8.imprint","IMPRINT",EDGE,{"disambiguationData":[TD([[subQ2,1.0]])],"derivedFrom":subQ1}),-1.0]])]});}
            var Q46;
            {var subQ0=sQuery(id+"F8.wireOp",EDGE,"E40");var subQ1=sQuery(id+"F8.wireOp",EDGE,"E29");var subQ2=makeQuery(id+"F8.imprint","INTERSECT",VERTEX,{"derivedFrom":[subQ1,subQ0]});Q46=makeQuery(id+"F8.imprint","IMPRINT",FACE,{"disambiguationData":[TD([[makeQuery(id+"F8.imprint","IMPRINT",EDGE,{"disambiguationData":[TD([[subQ2,1.0]])],"derivedFrom":subQ1}),-1.0]])]});}
            var Q47;
            {var subQ0=sQuery(id+"F8.wireOp",EDGE,"E41");var subQ1=sQuery(id+"F8.wireOp",EDGE,"E29");var subQ2=makeQuery(id+"F8.imprint","INTERSECT",VERTEX,{"derivedFrom":[subQ1,subQ0]});Q47=makeQuery(id+"F8.imprint","IMPRINT",FACE,{"disambiguationData":[TD([[makeQuery(id+"F8.imprint","IMPRINT",EDGE,{"disambiguationData":[TD([[subQ2,1.0]])],"derivedFrom":subQ1}),-1.0]])]});}
            var Q48;
            {var subQ0=sQuery(id+"F8.wireOp",EDGE,"E43");var subQ1=sQuery(id+"F8.wireOp",EDGE,"E29");var subQ2=makeQuery(id+"F8.imprint","INTERSECT",VERTEX,{"derivedFrom":[subQ1,subQ0]});Q48=makeQuery(id+"F8.imprint","IMPRINT",FACE,{"disambiguationData":[TD([[makeQuery(id+"F8.imprint","IMPRINT",EDGE,{"disambiguationData":[TD([[subQ2,-1.0]])],"derivedFrom":subQ1}),-1.0]])]});}
            var Q49;
            {var subQ0=sQuery(id+"F8.wireOp",EDGE,"E43");var subQ1=sQuery(id+"F8.wireOp",EDGE,"E29");var subQ2=makeQuery(id+"F8.imprint","INTERSECT",VERTEX,{"derivedFrom":[subQ1,subQ0]});Q49=makeQuery(id+"F8.imprint","IMPRINT",FACE,{"disambiguationData":[TD([[makeQuery(id+"F8.imprint","IMPRINT",EDGE,{"disambiguationData":[TD([[subQ2,1.0]])],"derivedFrom":subQ1}),-1.0]])]});}
            var Q50;
            {var subQ1=sQuery(id+"F8.wireOp",EDGE,"E31.bottom");var subQ20=sQuery(id+"F8.wireOp",EDGE,"E29");var subQ24=makeQuery(id+"F8.imprint","INTERSECT",VERTEX,{"disambiguationData":[OD(0.0)],"derivedFrom":[subQ20,subQ1]});Q50=makeQuery(id+"F8.imprint","IMPRINT",FACE,{"disambiguationData":[TD([[makeQuery(id+"F8.imprint","IMPRINT",EDGE,{"disambiguationData":[TD([[subQ24,-1.0]])],"derivedFrom":subQ20}),-1.0]])]});}
            extrude(context, id + "F9", {"entities" : qUnion([Q0, Q1, Q2, Q3, Q4, Q5, Q6, Q7, Q8, Q9, Q10, Q11, Q12, Q13, Q14, Q15, Q16, Q17, Q18, Q19, Q20, Q21, Q22, Q23, Q24, Q25, Q26, Q27, Q28, Q29, Q30, Q31, Q32, Q33, Q34, Q35, Q36, Q37, Q38, Q39, Q40, Q41, Q42, Q43, Q44, Q45, Q46, Q47, Q48, Q49, Q50]), "operationType" : NewBodyOperationType.ADD, "depth" : 1 * mm});
        }
        {
            var Q0;
            Q0=makeQuery(id+"F9.opExtrude","CAP_FACE",FACE,{"disambiguationData":[OSD([sQuery(id+"F8.wireOp",EDGE,"E29"),sQuery(id+"F8.wireOp",EDGE,"E30"),sQuery(id+"F8.wireOp",EDGE,"E31.bottom")])],"isStart":false});
            var sketch = newSketch(context, id + "F10", { "sketchPlane" : qUnion([Q0])});
            skLineSegment(sketch, "E53.0", {"start": v(31.76, 16.35) * mm, "end": v(38.2, 16.35) * mm});
            skLineSegment(sketch, "E54.0", {"start": v(31.76, 16.35) * mm, "end": v(31.76, 15.33) * mm});
            skLineSegment(sketch, "E55.0", {"start": v(31.76, 15.33) * mm, "end": v(38.2, 15.33) * mm});
            skLineSegment(sketch, "E56.0", {"start": v(38.2, 16.35) * mm, "end": v(38.2, 15.33) * mm});
            skLineSegment(sketch, "E57", {"start": v(31.76, 16.25) * mm, "end": v(38.2, 16.25) * mm});
            skSolve(sketch);
        }
        {
            var Q0;
            {var subQ0=sQuery(id+"F10.wireOp",EDGE,"E55.0");Q0=makeQuery(id+"F10.imprint","IMPRINT",FACE,{"disambiguationData":[TD([[makeQuery(id+"F10.imprint","IMPRINT",EDGE,{"derivedFrom":subQ0}),1.0]])]});}
            extrude(context, id + "F11", {"entities" : qUnion([Q0]), "operationType" : NewBodyOperationType.REMOVE, "oppositeDirection" : true, "depth" : 1 * mm});
        }
        {
            var Q0;
            Q0=makeQuery(id+"F4.opExtrude","SWEPT_EDGE",EDGE,{"disambiguationData":[OSD([sQuery(id+"F3.wireOp",EDGE,"E21"),sQuery(id+"F3.wireOp",EDGE,"E28.bottom"),sQuery(id+"F3.wireOp",EDGE,"E10")])]});
            fillet(context, id + "F12", {"entities" : qUnion([Q0]), "radius" : 5 * mm, "tangentPropagation" : true, "allowEdgeOverflow" : false});
        }
    });
